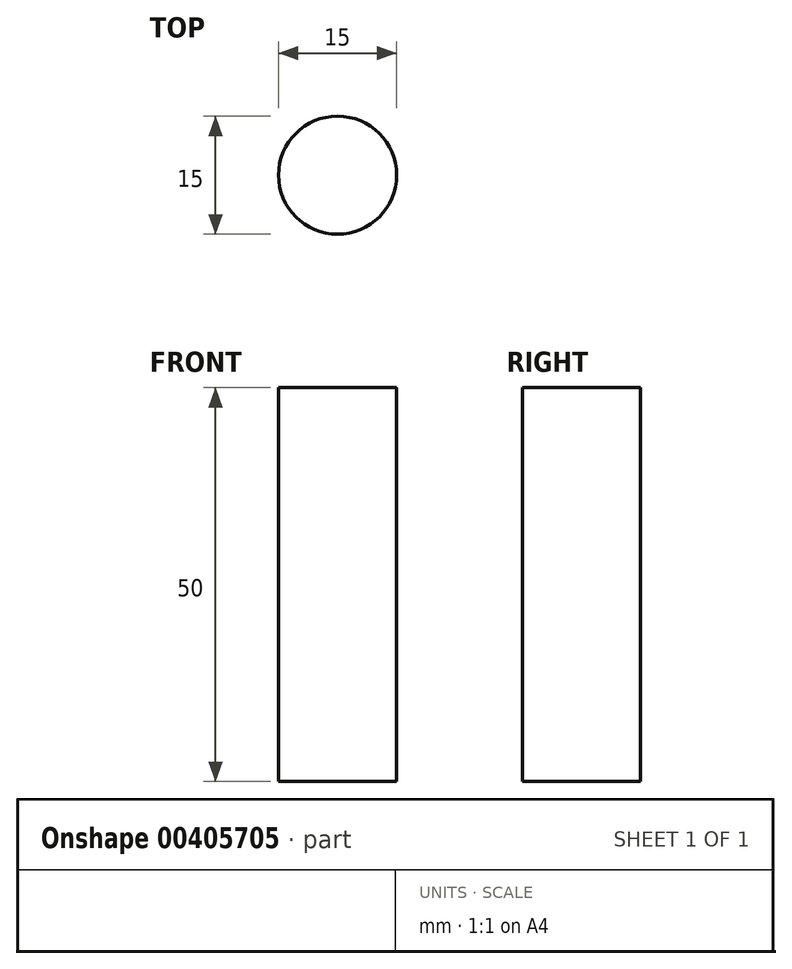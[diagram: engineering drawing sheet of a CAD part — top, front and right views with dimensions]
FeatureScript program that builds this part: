
annotation { "Feature Type Name" : "Feature", "Feature Type Description" : "" }
export const myFeature = defineFeature(function(context is Context, id is Id, definition is map)
    precondition{}
    {
        {
            var Q0;
            Q0=qCreatedBy(makeId("Top.planeOp"),FACE);
            var sketch = newSketch(context, id + "F0", { "sketchPlane" : qUnion([Q0])});
            skCircle(sketch, "E0", {"center": v(0, 0) * mm, "radius": 7.5 * mm});
            skSolve(sketch);
        }
        {
            var Q0;
            Q0=makeQuery(id+"F0.imprint","IMPRINT",FACE,{"disambiguationData":[TD([[makeQuery(id+"F0.imprint","IMPRINT",EDGE,{"derivedFrom":sQuery(id+"F0.wireOp",EDGE,"E0")}),1.0]])]});
            extrude(context, id + "F1", {"entities" : qUnion([Q0]), "depth" : 50 * mm});
        }
    });
